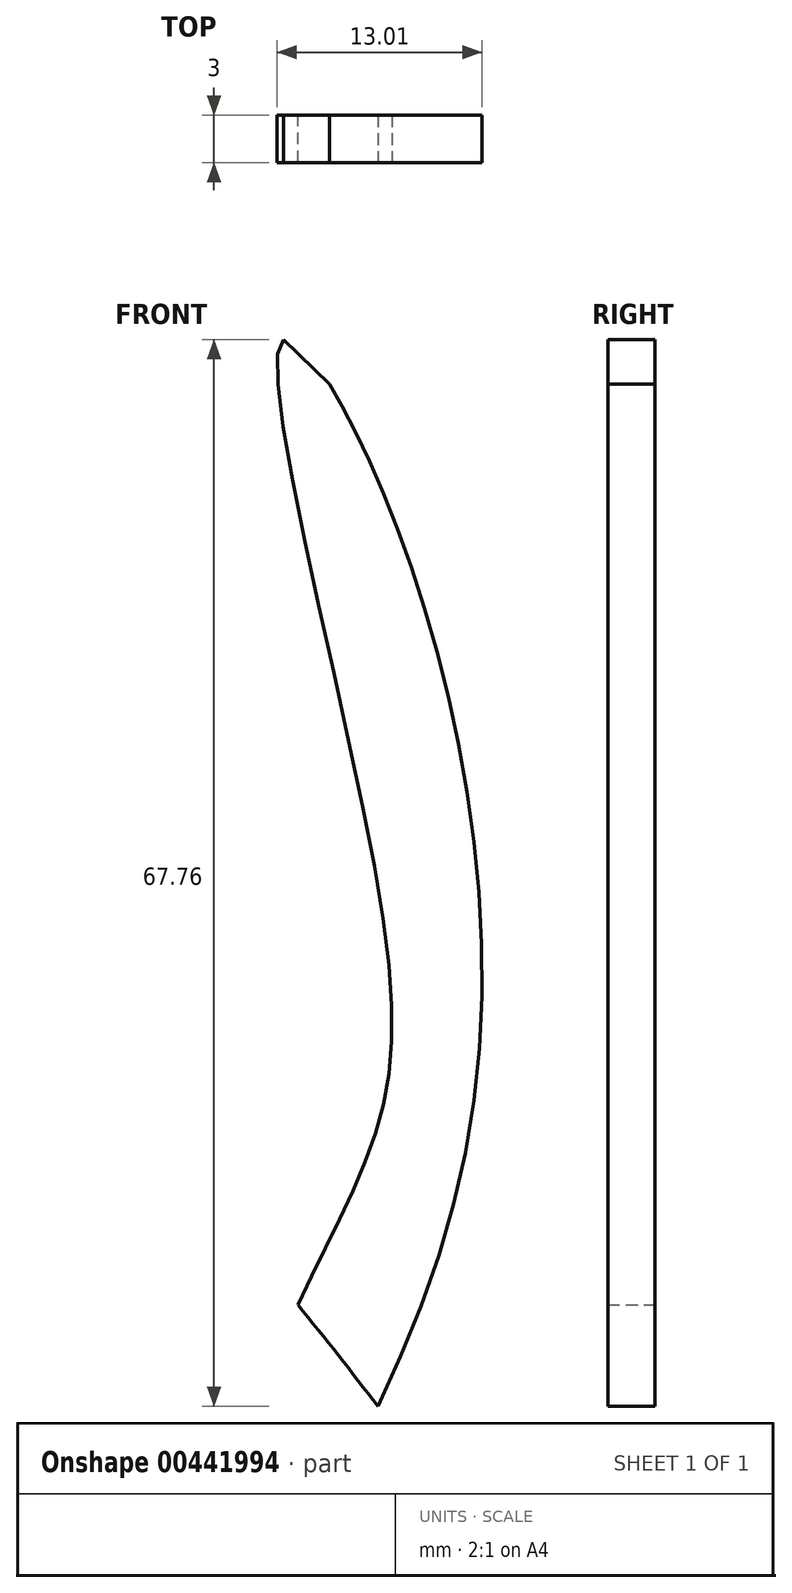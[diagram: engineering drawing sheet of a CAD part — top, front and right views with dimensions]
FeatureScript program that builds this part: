
annotation { "Feature Type Name" : "Feature", "Feature Type Description" : "" }
export const myFeature = defineFeature(function(context is Context, id is Id, definition is map)
    precondition{}
    {
        {
            var Q0;
            Q0=qCreatedBy(makeId("Front.planeOp"),FACE);
            var sketch = newSketch(context, id + "F0", { "sketchPlane" : qUnion([Q0])});
            skLineSegment(sketch, "E0.MirrorCS", {"start": v(-35.28, 430.56) * mm, "end": v(-38.2, 433.39) * mm});
            skLineSegment(sketch, "E1.MirrorCS", {"start": v(-86.84, 377.37) * mm, "end": v(-86.9, 375.8) * mm});
            skPoint(sketch, "E2.end.orphan", {"position": v(0, 0) * mm});
            skFitSpline(sketch, "E3", {"points": [v(-61.48, 455.88) * mm, v(-78.54, 415.46) * mm, v(-28.51, 339.42) * mm, v(-81.87, 181.34) * mm, v(-13.84, 0) * mm, v(-45.19, 65.28) * mm, v(-71.2, 145.99) * mm, v(-70.54, 202.68) * mm, v(-26.51, 303.4) * mm, v(-20.51, 346.75) * mm, v(-67.2, 406.78) * mm, v(-71.87, 427.46) * mm, v(-61.48, 455.88) * mm]});
            skFitSpline(sketch, "E4", {"points": [v(-38.2, 433.39) * mm, v(-26.51, 382.39) * mm, v(-78.54, 283.58) * mm, v(-16.6, 158.77) * mm, v(-92.32, 0) * mm, v(-67.2, 41.3) * mm, v(-35.87, 100.2) * mm, v(-26.51, 154.32) * mm, v(-45.19, 208.74) * mm, v(-71.87, 243.48) * mm, v(-84.06, 272.16) * mm, v(-84.06, 303.4) * mm, v(-45.19, 356.85) * mm, v(-37.28, 372.07) * mm, v(-32.42, 382.76) * mm, v(-32.42, 399.97) * mm, v(-38.2, 433.39) * mm]});
            skFitSpline(sketch, "E5", {"points": [v(-36.55, 0) * mm, v(-73.73, 72.75) * mm, v(-17.28, 227.42) * mm, v(-86.84, 377.37) * mm, v(-46.88, 301.48) * mm, v(-26.23, 233.78) * mm, v(-40, 157.52) * mm, v(-76.48, 98.11) * mm, v(-83.37, 50.7) * mm, v(-57.2, 12.8) * mm, v(-36.55, 0) * mm]});
            skLineSegment(sketch, "E6.trimOffspring", {"start": v(-61.38, 455.78) * mm, "end": v(-61.48, 455.88) * mm});
            skSolve(sketch);
        }
        {
            var Q0;
            {var subQ8=sQuery(id+"F0.wireOp",EDGE,"E0.MirrorCS");Q0=makeQuery(id+"F0.imprint","IMPRINT",FACE,{"disambiguationData":[TD([[makeQuery(id+"F0.imprint","IMPRINT",EDGE,{"derivedFrom":subQ8}),1.0]])]});}
            extrude(context, id + "F1", {"entities" : qUnion([Q0]), "depth" : 3 * mm, "offsetDistance" : 25 * mm});
        }
    });
